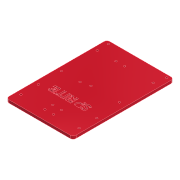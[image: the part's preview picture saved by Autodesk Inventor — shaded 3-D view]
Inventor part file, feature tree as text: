
AUTODESK INVENTOR PART (.ipt)
format: ipt  version: 2022 (Build 260153000, 153)  size: 275,456 bytes
history: native  units: mm
features: hole x4, sketch x3, extrude x2, fillet x1
ambient origin geometry x8: Origin, YZ Plane, XZ Plane, XY Plane, X Axis, Y Axis, Z Axis, Center Point
bodies: Solid1 (feature_tree)
feature tree (10):
  extrude  "Base"  TaperAngle=0.0deg  [1 undecoded]
  hole  "Mounting Holes"  [1 undecoded]
  fillet  "Fillet1"  Radius=50.0mm
  hole  "RasPi Mounting Holes"  [1 undecoded]
  hole  "LM2596 Mounting Holes"  [1 undecoded]
  hole  "Camera Mount Mounting Holes"  [1 undecoded]
  extrude  "SP RITE Logo"  Depth=2.0mm
  sketch  "Sketch11"  dims[d2=115.0mm d4=0.0mm]
  sketch  "Sketch15"  dims[d21=5.0mm d91=18.0mm d92=50.0mm]
  sketch  "Sketch16"  dims[d93=5.0mm d94=50.0mm d95=3.4mm d96=6.0mm d97=4.0mm d98=2.0mm d99=90.0deg d100=6.0mm d101=0.0mm d104=58.0mm d105=3.4mm d106=6.0mm d107=4.0mm d108=2.0mm d109=90.0deg d110=6.0mm d111=0.0mm d112=40.0mm d113=30.0mm d122=32.0mm d123=61.5mm d125=3.4mm d126=6.0mm d127=4.0mm d128=2.0mm d129=90.0deg d130=6.0mm d131=0.0mm d132=15.0mm d133=13.5mm d135=3.4mm d136=6.0mm d137=4.0mm d138=2.0mm d139=90.0deg d140=6.0mm d141=0.0mm d223=2.0mm d224=0.0mm d263=24.0mm d264=16.5mm d266=49.0mm d267=7.0mm d240=0.5mm d241=0.872665mm d242=0.5mm d243=0.872665mm]
note: 5 required parameter values undecoded (feature->parameter linkage not recoverable at this tier; creation-order binding heuristic only, values carry confidence <= 0.55)
